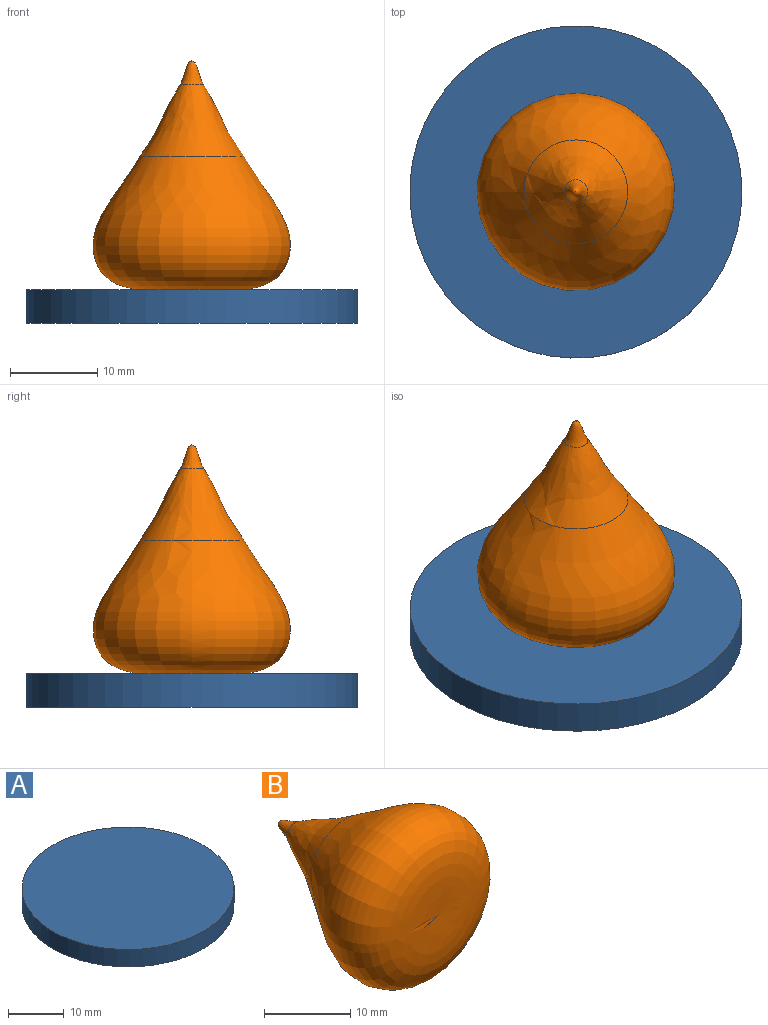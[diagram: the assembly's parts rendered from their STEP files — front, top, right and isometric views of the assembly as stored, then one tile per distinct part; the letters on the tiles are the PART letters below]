
ASSEMBLY  parts=2 mates=1
PART A: 3 faces, bbox 38.1x38.1x3.8 mm
  f0: cylinder r=19.05mm len=38.1mm, axis (0,0,-1), area 456mm2, adj f1,f2
  f1: plane 38.1x38.1mm, normal (0,0,1), area 1140.1mm2, adj f0
  f2: plane 38.1x38.1mm, normal (0,0,-1), area 1140.1mm2, adj f0
PART B: 3 faces, bbox 22.7x26.4x22.7 mm
  f0: revolved ~2.72x2.71mm, area 15mm2, adj f1
  f1: revolved ~11.9x11.9mm, area 211.6mm2, adj f0,f2
  f2: revolved ~22.66x22.66mm, area 1265.3mm2, adj f1
PLACE A t=(-43.51,-80.5,-17.15)mm
PLACE B rot(axis=(1,0,0),90deg) t=(-33.98,-35.29,73.59)mm
MATE fastened B.f0 <-> A.f0  axis (0,0,1) through (-43.51,-35.29,-13.34)mm
